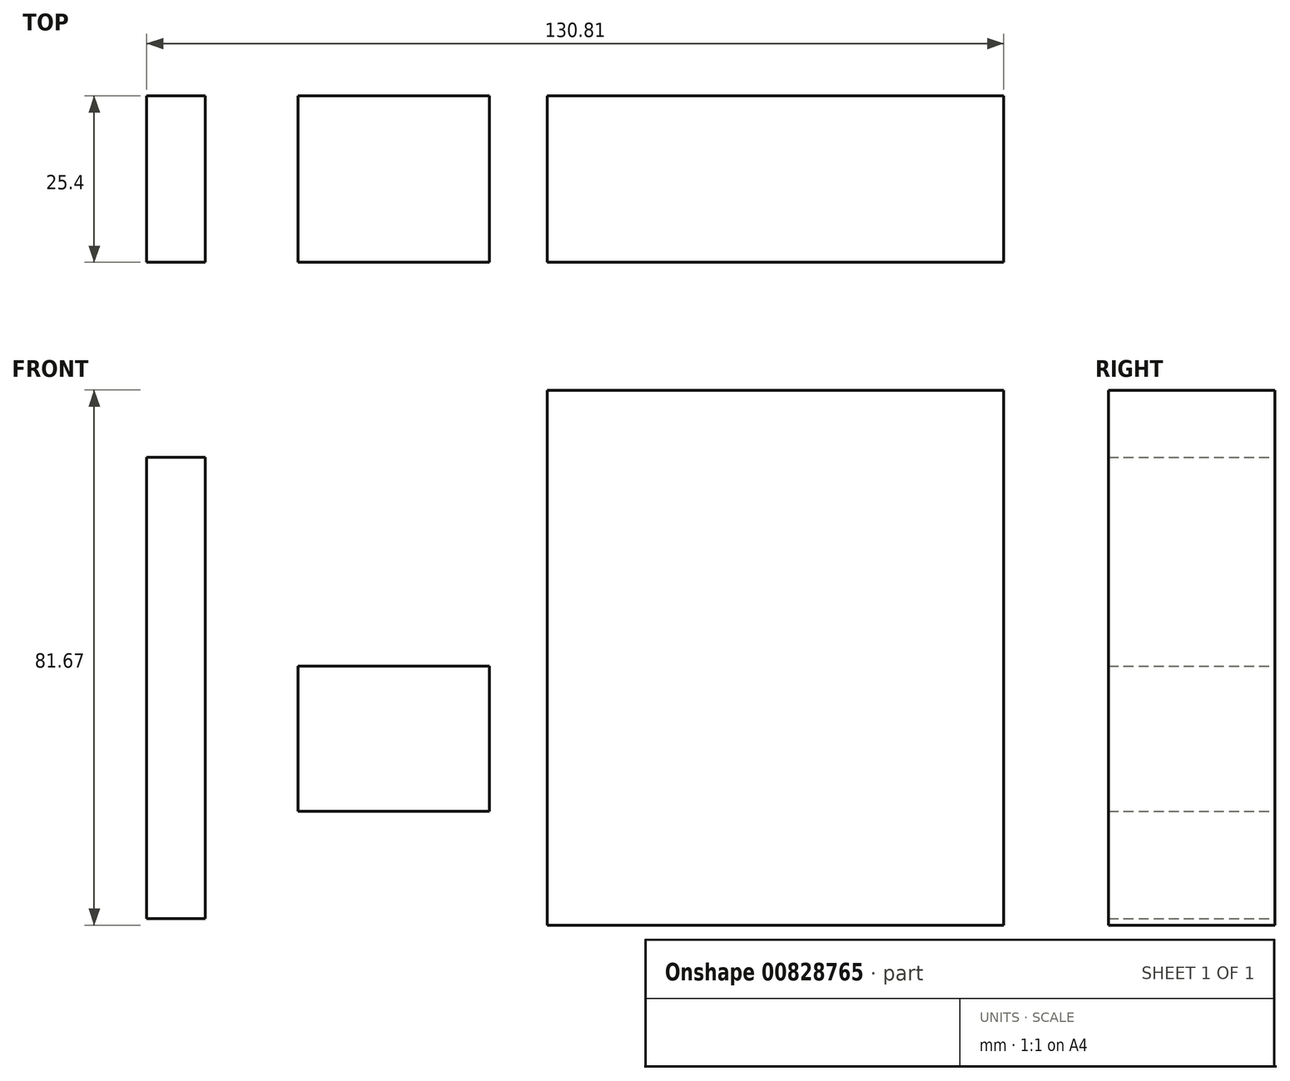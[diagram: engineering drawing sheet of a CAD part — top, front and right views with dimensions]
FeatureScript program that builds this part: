
annotation { "Feature Type Name" : "Feature", "Feature Type Description" : "" }
export const myFeature = defineFeature(function(context is Context, id is Id, definition is map)
    precondition{}
    {
        {
            var Q0;
            Q0=qCreatedBy(makeId("Front.planeOp"),FACE);
            var sketch = newSketch(context, id + "F0", { "sketchPlane" : qUnion([Q0])});
            skLineSegment(sketch, "E0.bottom", {"start": v(-26.17, 38.47) * mm, "end": v(43.51, 38.47) * mm});
            skLineSegment(sketch, "E0.top", {"start": v(-26.17, -43.2) * mm, "end": v(43.51, -43.2) * mm});
            skLineSegment(sketch, "E0.left", {"start": v(-26.17, 38.47) * mm, "end": v(-26.17, -43.2) * mm});
            skLineSegment(sketch, "E0.right", {"start": v(43.51, 38.47) * mm, "end": v(43.51, -43.2) * mm});
            skLineSegment(sketch, "E1.bottom", {"start": v(-78.35, 28.23) * mm, "end": v(-87.3, 28.23) * mm});
            skLineSegment(sketch, "E1.top", {"start": v(-78.35, -42.23) * mm, "end": v(-87.3, -42.23) * mm});
            skLineSegment(sketch, "E1.left", {"start": v(-78.35, 28.23) * mm, "end": v(-78.35, -42.23) * mm});
            skLineSegment(sketch, "E1.right", {"start": v(-87.3, 28.23) * mm, "end": v(-87.3, -42.23) * mm});
            skLineSegment(sketch, "E2.bottom", {"start": v(-64.2, -3.65) * mm, "end": v(-34.98, -3.65) * mm});
            skLineSegment(sketch, "E2.top", {"start": v(-64.2, -25.8) * mm, "end": v(-34.98, -25.8) * mm});
            skLineSegment(sketch, "E2.left", {"start": v(-64.2, -3.65) * mm, "end": v(-64.2, -25.8) * mm});
            skLineSegment(sketch, "E2.right", {"start": v(-34.98, -3.65) * mm, "end": v(-34.98, -25.8) * mm});
            skSolve(sketch);
        }
        {
            var Q0;
            Q0 = qSketchRegion(id + "F0", true);
            extrude(context, id + "F1", {"entities" : qUnion([Q0]), "depth" : 25.4 * mm, "offsetDistance" : 25.4 * mm});
        }
    });
